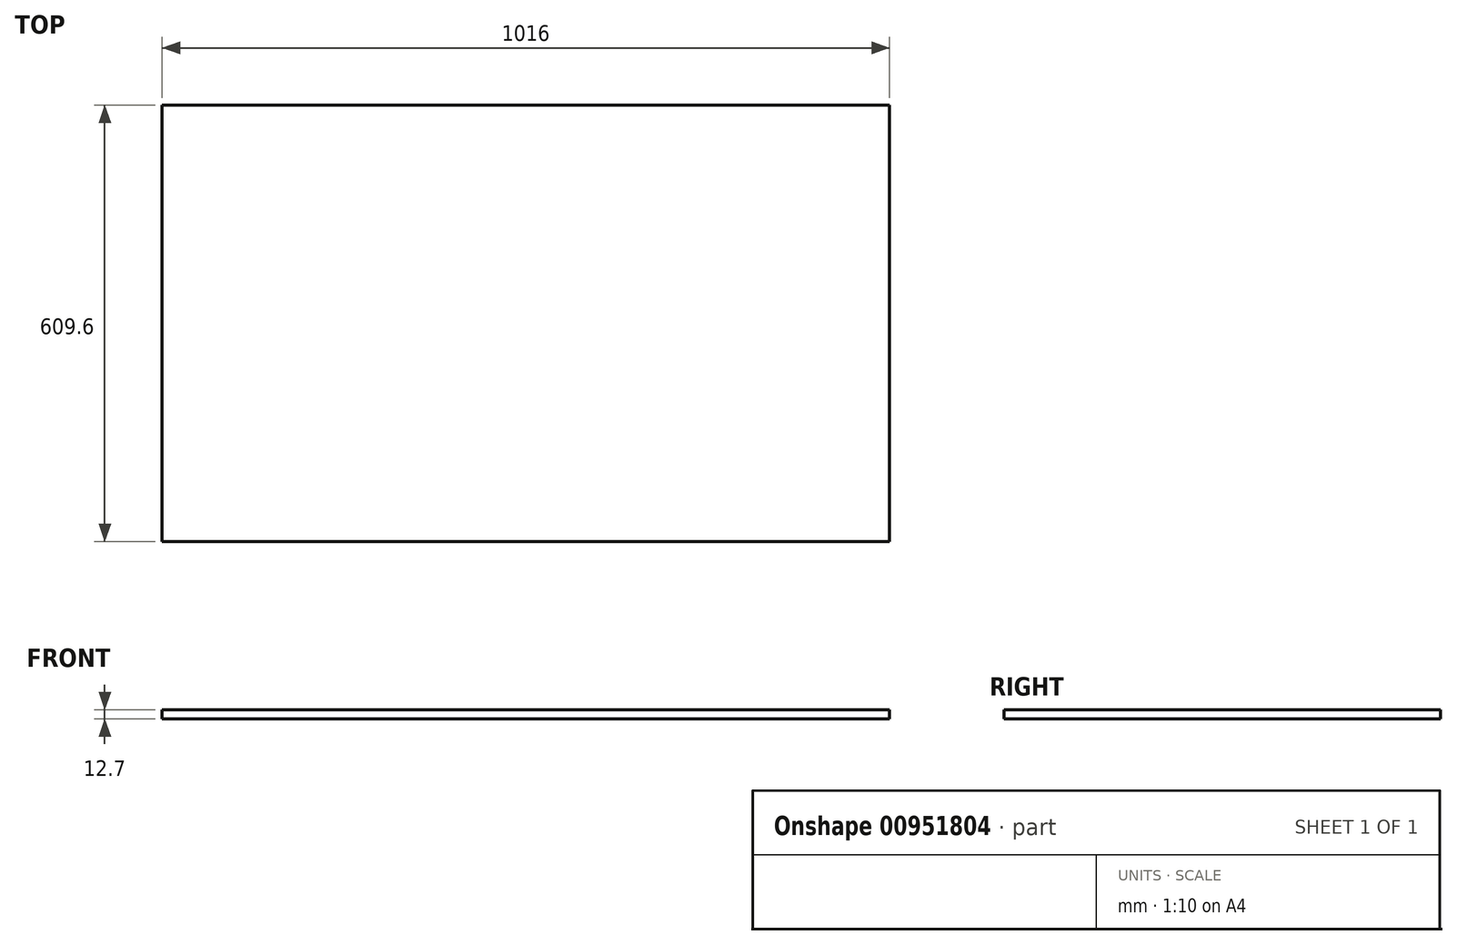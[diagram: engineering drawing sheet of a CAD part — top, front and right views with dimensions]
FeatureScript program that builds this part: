
annotation { "Feature Type Name" : "Feature", "Feature Type Description" : "" }
export const myFeature = defineFeature(function(context is Context, id is Id, definition is map)
    precondition{}
    {
        {
            var Q0;
            Q0=qCreatedBy(makeId("Top.planeOp"),FACE);
            var sketch = newSketch(context, id + "F0", { "sketchPlane" : qUnion([Q0])});
            skLineSegment(sketch, "E0.bottom", {"start": v(508, -304.8) * mm, "end": v(-508, -304.8) * mm});
            skLineSegment(sketch, "E0.top", {"start": v(508, 304.8) * mm, "end": v(-508, 304.8) * mm});
            skLineSegment(sketch, "E0.left", {"start": v(508, -304.8) * mm, "end": v(508, 304.8) * mm});
            skLineSegment(sketch, "E0.right", {"start": v(-508, -304.8) * mm, "end": v(-508, 304.8) * mm});
            skPoint(sketch, "E0.middle", {"position": v(0, 0) * mm});
            skSolve(sketch);
        }
        {
            var Q0;
            Q0 = qSketchRegion(id + "F0", true);
            extrude(context, id + "F1", {"entities" : qUnion([Q0]), "depth" : 12.7 * mm, "offsetDistance" : 25.4 * mm});
        }
    });
